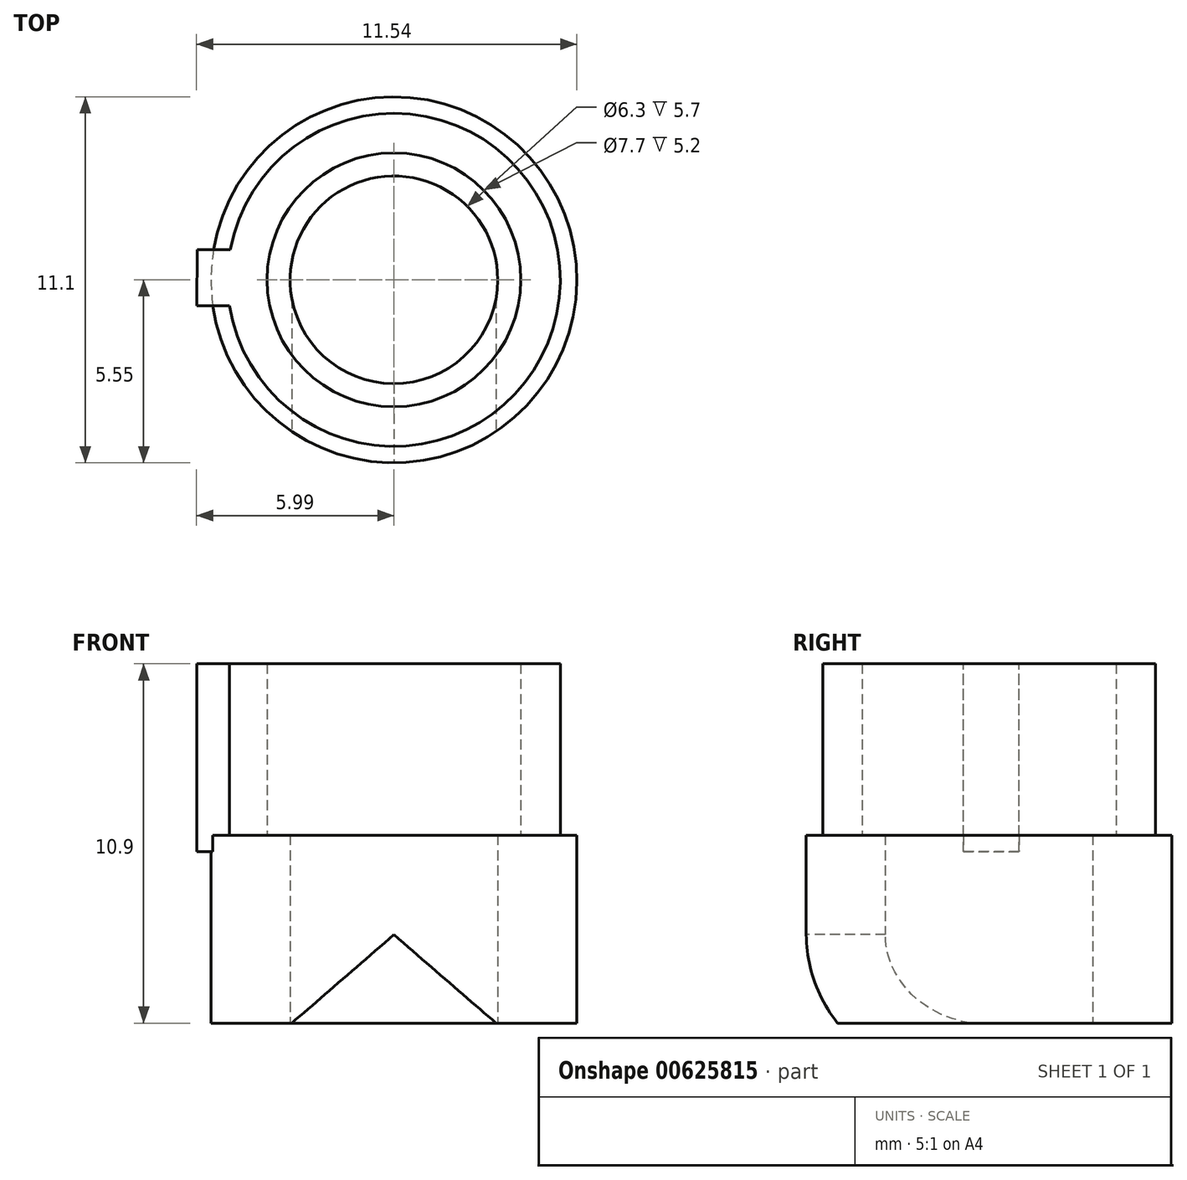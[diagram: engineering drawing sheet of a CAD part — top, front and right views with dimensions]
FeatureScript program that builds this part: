
annotation { "Feature Type Name" : "Feature", "Feature Type Description" : "" }
export const myFeature = defineFeature(function(context is Context, id is Id, definition is map)
    precondition{}
    {
        {
            var Q0;
            Q0=qCreatedBy(makeId("Top.planeOp"),FACE);
            var sketch = newSketch(context, id + "F0", { "sketchPlane" : qUnion([Q0])});
            skCircle(sketch, "E0", {"center": v(0, 0) * mm, "radius": 5.55 * mm});
            skCircle(sketch, "E1", {"center": v(0, 0) * mm, "radius": 3.15 * mm});
            skSolve(sketch);
        }
        {
            var Q0;
            Q0 = qSketchRegion(id + "F0", true);
            extrude(context, id + "F1", {"entities" : qUnion([Q0]), "depth" : 5.7 * mm, "offsetDistance" : 25 * mm});
        }
        {
            var Q0;
            Q0=makeQuery(id+"F1.opExtrude","CAP_FACE",FACE,{"disambiguationData":[OSD([sQuery(id+"F0.wireOp",EDGE,"E0"),sQuery(id+"F0.wireOp",EDGE,"E1")])],"isStart":false});
            var sketch = newSketch(context, id + "F2", { "sketchPlane" : qUnion([Q0])});
            skPoint(sketch, "E2.0", {"position": v(0, 0) * mm});
            skCircle(sketch, "E3", {"center": v(0, 0) * mm, "radius": 3.85 * mm});
            skCircle(sketch, "E4.0", {"center": v(0, 0) * mm, "radius": 5.05 * mm});
            skSolve(sketch);
        }
        {
            var Q0;
            Q0=makeQuery(id+"F2.imprint","IMPRINT",FACE,{"disambiguationData":[TD([[makeQuery(id+"F2.imprint","IMPRINT",EDGE,{"derivedFrom":sQuery(id+"F2.wireOp",EDGE,"E3")}),-1.0]])]});
            extrude(context, id + "F3", {"entities" : qUnion([Q0]), "operationType" : NewBodyOperationType.ADD, "depth" : 5.2 * mm, "offsetDistance" : 25 * mm});
        }
        {
            var Q0;
            Q0=qCreatedBy(makeId("Front.planeOp"),FACE);
            cPlane(context, id + "F4", {"entities" : qUnion([Q0]), "cplaneType" : CPlaneType.OFFSET, "offset" : 25 * mm, "width" : 150 * mm, "height" : 150 * mm});
        }
        {
            var Q0;
            Q0=qCreatedBy(id+"F4.planeOp",FACE);
            var sketch = newSketch(context, id + "F5", { "sketchPlane" : qUnion([Q0])});
            skLineSegment(sketch, "E5", {"start": v(3.1, 0) * mm, "end": v(0, 2.68) * mm});
            skLineSegment(sketch, "E6", {"start": v(0, 2.68) * mm, "end": v(-3.1, 0) * mm});
            skLineSegment(sketch, "E7", {"start": v(-3.1, 0) * mm, "end": v(3.1, 0) * mm});
            skSolve(sketch);
        }
        {
            var Q0;
            Q0=makeQuery(id+"F5.imprint","IMPRINT",FACE,{"disambiguationData":[TD([[makeQuery(id+"F5.imprint","IMPRINT",EDGE,{"derivedFrom":sQuery(id+"F5.wireOp",EDGE,"E5")}),1.0]])]});
            extrude(context, id + "F6", {"entities" : qUnion([Q0]), "operationType" : NewBodyOperationType.REMOVE, "oppositeDirection" : true, "depth" : 25 * mm, "offsetDistance" : 25 * mm});
        }
        {
            var Q0;
            Q0=makeQuery(id+"F3.opExtrude","CAP_FACE",FACE,{"disambiguationData":[OSD([sQuery(id+"F2.wireOp",EDGE,"E3"),sQuery(id+"F2.wireOp",EDGE,"E4.0")])],"isStart":false});
            var sketch = newSketch(context, id + "F7", { "sketchPlane" : qUnion([Q0])});
            skLineSegment(sketch, "E8", {"start": v(-4.97, 0.91) * mm, "end": v(-5.97, 0.91) * mm});
            skLineSegment(sketch, "E9", {"start": v(-4.99, -0.79) * mm, "end": v(-5.99, -0.79) * mm});
            skLineSegment(sketch, "E10", {"start": v(-5.99, -0.79) * mm, "end": v(-5.97, 0.91) * mm});
            skSolve(sketch);
        }
        {
            var Q0;
            {var subQ0=sQuery(id+"F7.wireOp",EDGE,"E8");Q0=makeQuery(id+"F7.imprint","IMPRINT",FACE,{"disambiguationData":[TD([[makeQuery(id+"F7.imprint","IMPRINT",EDGE,{"derivedFrom":subQ0}),1.0]])]});}
            extrude(context, id + "F8", {"entities" : qUnion([Q0]), "operationType" : NewBodyOperationType.ADD, "oppositeDirection" : true, "depth" : 5.7 * mm, "offsetDistance" : 25 * mm});
        }
    });
